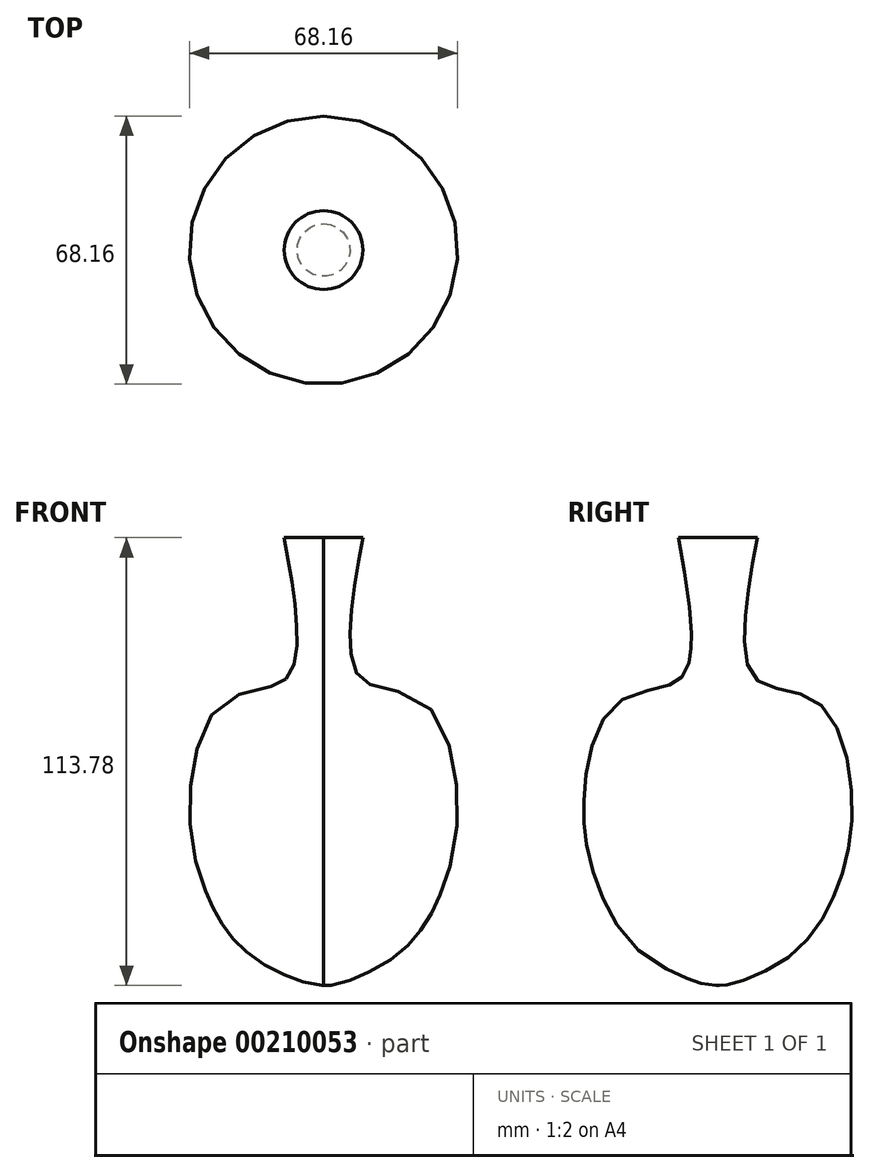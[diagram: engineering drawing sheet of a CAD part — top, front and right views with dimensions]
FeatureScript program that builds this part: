
annotation { "Feature Type Name" : "Feature", "Feature Type Description" : "" }
export const myFeature = defineFeature(function(context is Context, id is Id, definition is map)
    precondition{}
    {
        {
            var Q0;
            Q0=qCreatedBy(makeId("Right.planeOp"),FACE);
            var sketch = newSketch(context, id + "F0", { "sketchPlane" : qUnion([Q0])});
            skLineSegment(sketch, "E0", {"start": v(0, 41.73) * mm, "end": v(10, 41.73) * mm});
            skFitSpline(sketch, "E1", {"points": [v(10, 41.73) * mm, v(6.88, 20.16) * mm, v(10, 5.47) * mm, v(25.32, 0) * mm, v(34.07, -26.1) * mm, v(30, -47.98) * mm, v(18.75, -64.24) * mm, v(3.13, -71.74) * mm, v(0, -72.05) * mm], "startDerivative": vector(-27.81, -151.81) * mm, "endDerivative": vector(-46.04, 0.6) * mm});
            skLineSegment(sketch, "E2.MirrorCS", {"start": v(0, 41.73) * mm, "end": v(-10, 41.73) * mm});
            skFitSpline(sketch, "E3.MirrorCS", {"points": [v(-10, 41.73) * mm, v(-6.88, 20.16) * mm, v(-10, 5.47) * mm, v(-25.32, 0) * mm, v(-34.07, -26.1) * mm, v(-30, -47.98) * mm, v(-18.75, -64.24) * mm, v(-3.13, -71.74) * mm, v(0, -72.05) * mm], "startDerivative": vector(27.81, -151.81) * mm, "endDerivative": vector(46.04, 0.6) * mm});
            skPoint(sketch, "E4.orphan", {"position": v(0, 76.26) * mm});
            skPoint(sketch, "E5.start.orphan", {"position": v(0, 71.77) * mm});
            skPoint(sketch, "E6.start.orphan", {"position": v(0, 68.02) * mm});
            skLineSegment(sketch, "E7", {"start": v(0, 76.26) * mm, "end": v(0, -76.98) * mm});
            skSolve(sketch);
        }
        {
            var Q0;
            Q0=makeQuery(id+"F0.imprint","IMPRINT",FACE,{"disambiguationData":[TD([[makeQuery(id+"F0.imprint","IMPRINT",EDGE,{"derivedFrom":sQuery(id+"F0.wireOp",EDGE,"E0")}),-1.0]])]});
            var Q1;
            Q1=sQuery(id+"F0.wireOp",EDGE,"E7");
            revolve(context, id + "F1", {"entities" : qUnion([Q0]), "axis" : qUnion([Q1]), "revolveType" : RevolveType.FULL});
        }
    });
